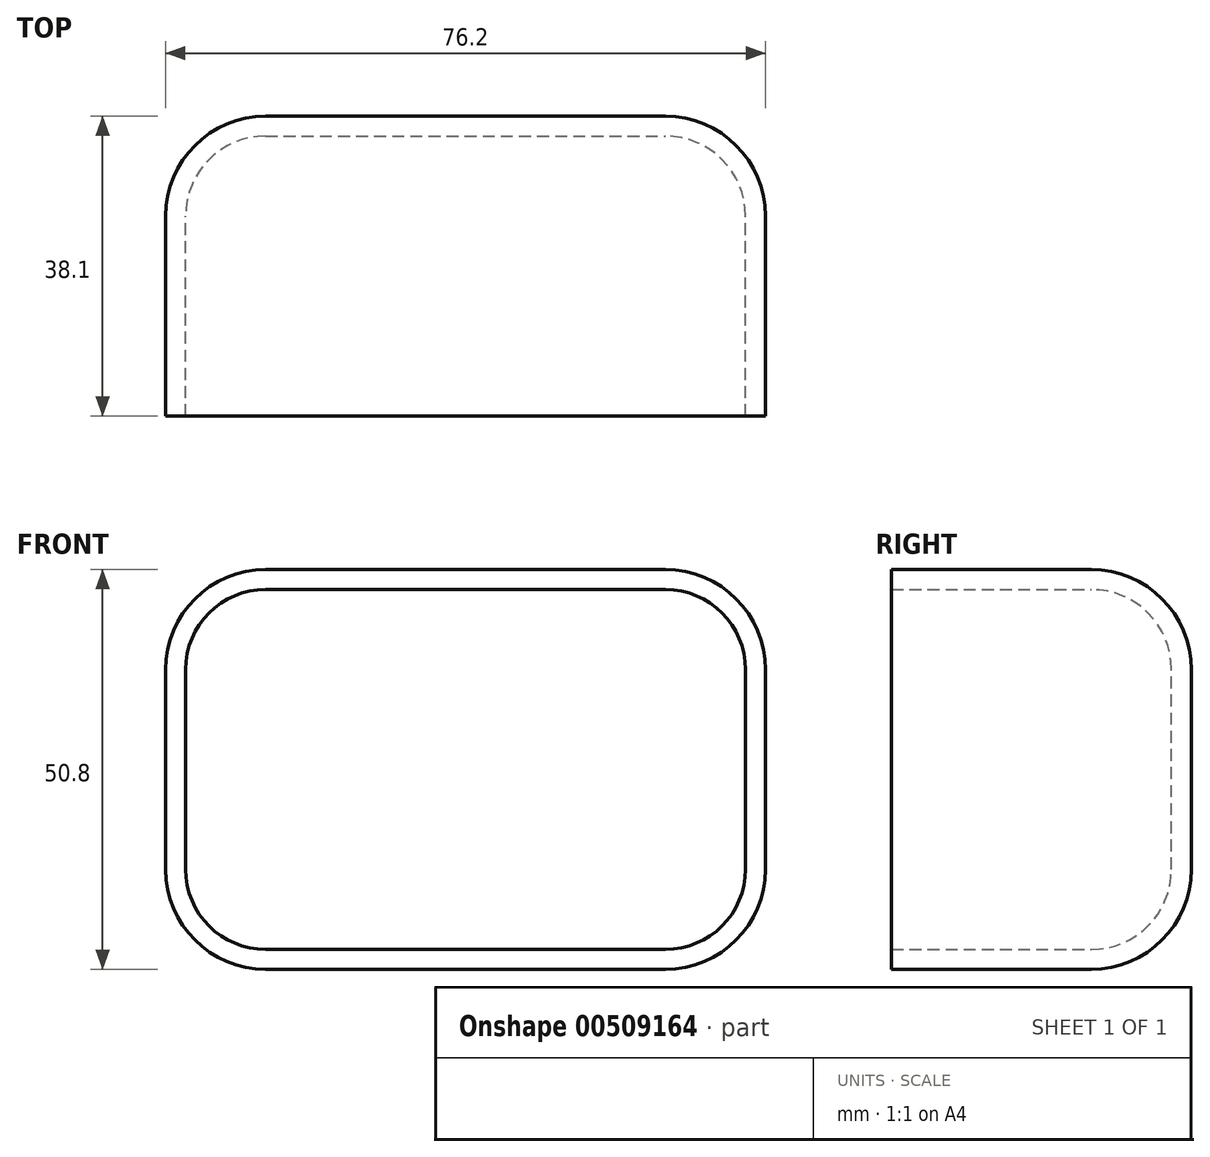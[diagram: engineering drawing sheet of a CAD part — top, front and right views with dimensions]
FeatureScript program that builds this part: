
annotation { "Feature Type Name" : "Feature", "Feature Type Description" : "" }
export const myFeature = defineFeature(function(context is Context, id is Id, definition is map)
    precondition{}
    {
        {
            var Q0;
            Q0=qCreatedBy(makeId("Front.planeOp"),FACE);
            var sketch = newSketch(context, id + "F0", { "sketchPlane" : qUnion([Q0])});
            skLineSegment(sketch, "E0.bottom", {"start": v(38.1, 25.4) * mm, "end": v(-38.1, 25.4) * mm});
            skLineSegment(sketch, "E0.top", {"start": v(38.1, -25.4) * mm, "end": v(-38.1, -25.4) * mm});
            skLineSegment(sketch, "E0.left", {"start": v(38.1, 25.4) * mm, "end": v(38.1, -25.4) * mm});
            skLineSegment(sketch, "E0.right", {"start": v(-38.1, 25.4) * mm, "end": v(-38.1, -25.4) * mm});
            skPoint(sketch, "E0.middle", {"position": v(0, 0) * mm});
            skSolve(sketch);
        }
        {
            var Q0;
            Q0=makeQuery(id+"F0.imprint","IMPRINT",FACE,{"disambiguationData":[TD([[makeQuery(id+"F0.imprint","IMPRINT",EDGE,{"derivedFrom":sQuery(id+"F0.wireOp",EDGE,"E0.bottom")}),1.0]])]});
            var Q1;
            Q1=sQuery(id+"F0.wireOp",EDGE,"E0.bottom");
            var Q2;
            Q2=sQuery(id+"F0.wireOp",EDGE,"E0.right");
            var Q3;
            Q3=sQuery(id+"F0.wireOp",EDGE,"E0.left");
            var Q4;
            Q4=sQuery(id+"F0.wireOp",EDGE,"E0.top");
            extrude(context, id + "F1", {"entities" : qUnion([Q0]), "surfaceEntities" : qUnion([Q1, Q2, Q3, Q4]), "depth" : 38.1 * mm});
        }
        {
            var Q0;
            Q0=makeQuery(id+"F1.opExtrude","SWEPT_EDGE",EDGE,{"disambiguationData":[OSD([sQuery(id+"F0.wireOp",EDGE,"E0.bottom"),sQuery(id+"F0.wireOp",EDGE,"E0.left")])]});
            var Q1;
            Q1=makeQuery(id+"F1.opExtrude","SWEPT_EDGE",EDGE,{"disambiguationData":[OSD([sQuery(id+"F0.wireOp",EDGE,"E0.top"),sQuery(id+"F0.wireOp",EDGE,"E0.left")])]});
            var Q2;
            Q2=makeQuery(id+"F1.opExtrude","SWEPT_EDGE",EDGE,{"disambiguationData":[OSD([sQuery(id+"F0.wireOp",EDGE,"E0.bottom"),sQuery(id+"F0.wireOp",EDGE,"E0.right")])]});
            var Q3;
            Q3=makeQuery(id+"F1.opExtrude","SWEPT_EDGE",EDGE,{"disambiguationData":[OSD([sQuery(id+"F0.wireOp",EDGE,"E0.top"),sQuery(id+"F0.wireOp",EDGE,"E0.right")])]});
            fillet(context, id + "F2", {"entities" : qUnion([Q0, Q1, Q2, Q3]), "radius" : 12.7 * mm, "tangentPropagation" : true, "allowEdgeOverflow" : false});
        }
        {
            var Q0;
            Q0=makeQuery(id+"F1.opExtrude","CAP_EDGE",EDGE,{"disambiguationData":[OSD([sQuery(id+"F0.wireOp",EDGE,"E0.bottom")])],"isStart":true});
            fillet(context, id + "F3", {"entities" : qUnion([Q0]), "radius" : 12.7 * mm, "tangentPropagation" : true, "allowEdgeOverflow" : false});
        }
        {
            var Q0;
            Q0=makeQuery(id+"F1.opExtrude","CAP_FACE",FACE,{"disambiguationData":[OSD([sQuery(id+"F0.wireOp",EDGE,"E0.bottom"),sQuery(id+"F0.wireOp",EDGE,"E0.top"),sQuery(id+"F0.wireOp",EDGE,"E0.left"),sQuery(id+"F0.wireOp",EDGE,"E0.right")])],"isStart":false});
            shell(context, id + "F4", {"entities" : qUnion([Q0]), "thickness" : 2.54 * mm});
        }
    });
